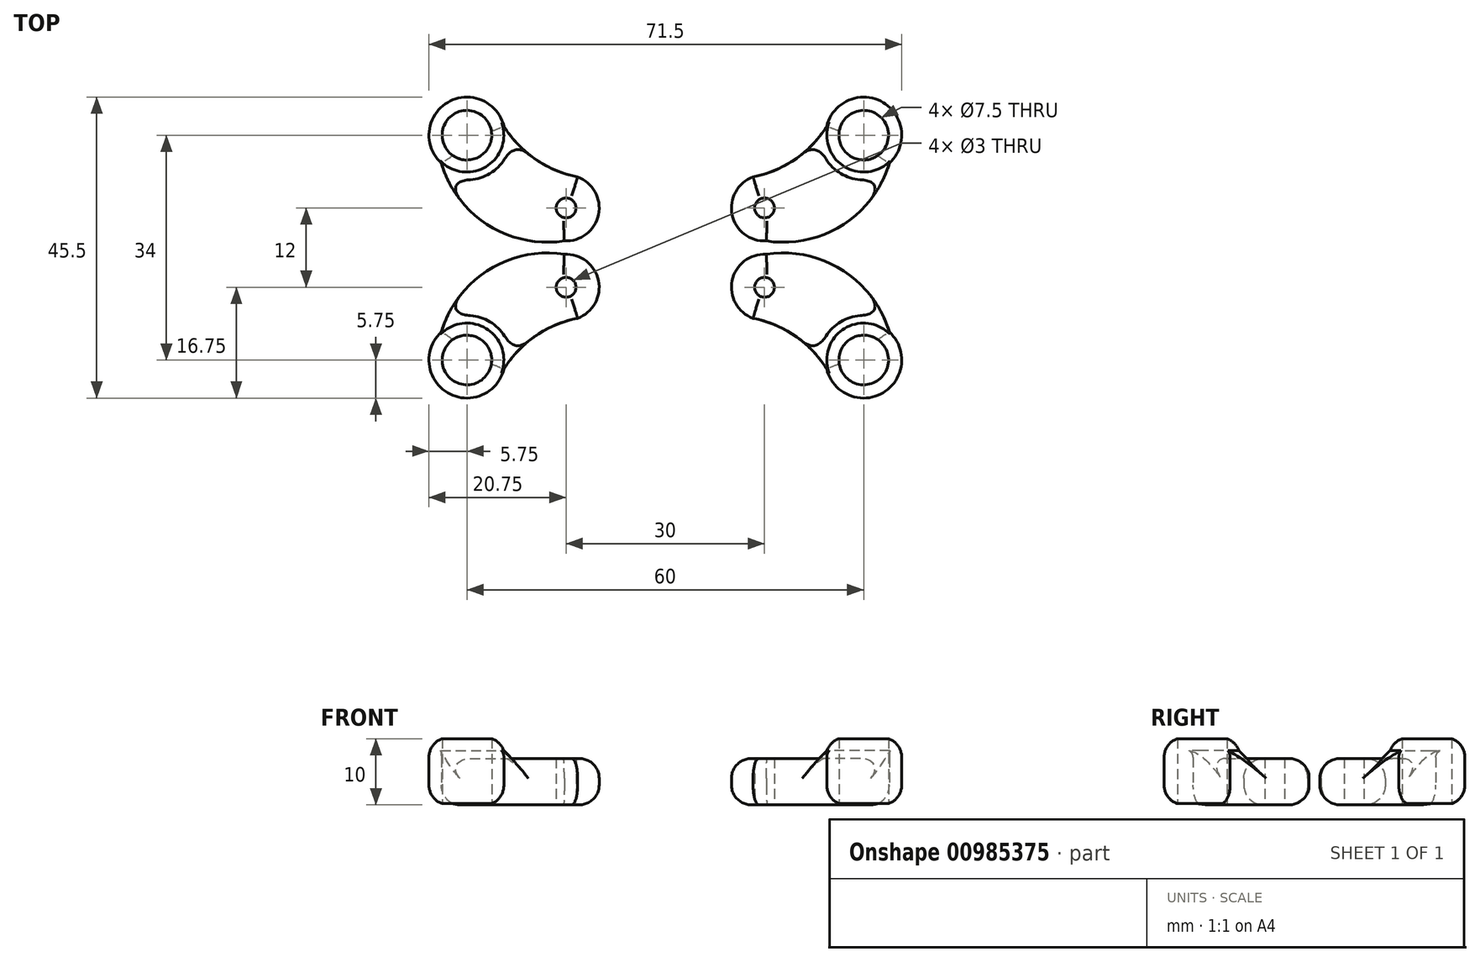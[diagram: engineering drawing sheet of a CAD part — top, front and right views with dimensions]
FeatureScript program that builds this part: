
annotation { "Feature Type Name" : "Feature", "Feature Type Description" : "" }
export const myFeature = defineFeature(function(context is Context, id is Id, definition is map)
    precondition{}
    {
        {
            var Q0;
            Q0=qCreatedBy(makeId("Top.planeOp"),FACE);
            var sketch = newSketch(context, id + "F0", { "sketchPlane" : qUnion([Q0])});
            skPoint(sketch, "E0.middle", {"position": v(0, 0) * mm});
            skCircle(sketch, "E1", {"center": v(-30, 17) * mm, "radius": 3.75 * mm});
            skCircle(sketch, "E2", {"center": v(-30, 17) * mm, "radius": 5.75 * mm});
            skCircle(sketch, "E3", {"center": v(-15, 6) * mm, "radius": 1.5 * mm});
            skCircle(sketch, "E4", {"center": v(-15, 6) * mm, "radius": 5 * mm});
            skArc(sketch, "E5", {"start": v(-25.68, 20.8) * mm, "mid": v(-20.74, 14.2) * mm, "end": v(-13.27, 10.7) * mm});
            skArc(sketch, "E6", {"start": v(-33.87, 12.75) * mm, "mid": v(-26.77, 3.4) * mm, "end": v(-15.27, 1) * mm});
            skSolve(sketch);
        }
        {
            var Q0;
            Q0=makeQuery(id+"F0.imprint","IMPRINT",FACE,{"disambiguationData":[TD([[makeQuery(id+"F0.imprint","IMPRINT",EDGE,{"derivedFrom":sQuery(id+"F0.wireOp",EDGE,"9357O7tW-9z78-CaA4-5se2-U8UIPOlfQfit.bottom")}),1.0]])]});
            var Q1;
            Q1=makeQuery(id+"F0.imprint","IMPRINT",FACE,{"disambiguationData":[TD([[makeQuery(id+"F0.imprint","IMPRINT",EDGE,{"derivedFrom":sQuery(id+"F0.wireOp",EDGE,"9357O7tW-9z78-CaA4-5se2-U8UIPOlfQfit.bottom")}),-1.0]])]});
            var Q2;
            {var subQ0=sQuery(id+"F0.wireOp",EDGE,"XfmaCdGe-Nsh5-LR8N-U050-nXJdRo87k7nu");Q2=makeQuery(id+"F0.imprint","IMPRINT",FACE,{"disambiguationData":[TD([[makeQuery(id+"F0.imprint","IMPRINT",EDGE,{"derivedFrom":subQ0}),-1.0]])]});}
            var Q3;
            {var subQ0=sQuery(id+"F0.wireOp",EDGE,"67c493aa-9df7-43f4-b791-e47cdcb916b60.MirrorCS");Q3=makeQuery(id+"F0.imprint","IMPRINT",FACE,{"disambiguationData":[TD([[makeQuery(id+"F0.imprint","IMPRINT",EDGE,{"derivedFrom":subQ0}),-1.0]])]});}
            var Q4;
            {var subQ0=sQuery(id+"F0.wireOp",EDGE,"3c266ea2-0ddf-4ded-b89f-077357a7d8e80.MirrorCS");Q4=makeQuery(id+"F0.imprint","IMPRINT",FACE,{"disambiguationData":[TD([[makeQuery(id+"F0.imprint","IMPRINT",EDGE,{"derivedFrom":subQ0}),-1.0]])]});}
            var Q5;
            {var subQ0=sQuery(id+"F0.wireOp",EDGE,"ab4d64e5-a29a-4c87-9f54-f3676ced8fba0.MirrorCS");Q5=makeQuery(id+"F0.imprint","IMPRINT",FACE,{"disambiguationData":[TD([[makeQuery(id+"F0.imprint","IMPRINT",EDGE,{"derivedFrom":subQ0}),1.0]])]});}
            var Q6;
            Q6=makeQuery(id+"F0.imprint","IMPRINT",FACE,{"disambiguationData":[TD([[makeQuery(id+"F0.imprint","IMPRINT",EDGE,{"derivedFrom":sQuery(id+"F0.wireOp",EDGE,"5d5cfb4f-1e90-434a-910e-95713f9e32be0.MirrorC")}),1.0]])]});
            var Q7;
            Q7=makeQuery(id+"F0.imprint","IMPRINT",FACE,{"disambiguationData":[TD([[makeQuery(id+"F0.imprint","IMPRINT",EDGE,{"derivedFrom":sQuery(id+"F0.wireOp",EDGE,"24c43ebd-9ed0-4dd5-8c82-3635907a6bdc0.MirrorC")}),-1.0]])]});
            var Q8;
            Q8=makeQuery(id+"F0.imprint","IMPRINT",FACE,{"disambiguationData":[TD([[makeQuery(id+"F0.imprint","IMPRINT",EDGE,{"derivedFrom":sQuery(id+"F0.wireOp",EDGE,"ed7e95fd-fa47-4424-be7c-35b6ced3335c0.MirrorC")}),1.0]])]});
            var Q9;
            Q9=makeQuery(id+"F0.imprint","IMPRINT",FACE,{"disambiguationData":[TD([[makeQuery(id+"F0.imprint","IMPRINT",EDGE,{"derivedFrom":sQuery(id+"F0.wireOp",EDGE,"sMkcqQPm-D7Am-9ELx-zUy6-8poXXiJyxJ4t")}),-1.0]])]});
            var Q10;
            {var subQ2=sQuery(id+"F0.wireOp",EDGE,"X9ugOP2y-zs2E-4G1d-y63R-nyf2ct76moEV");Q10=makeQuery(id+"F0.imprint","IMPRINT",FACE,{"disambiguationData":[TD([[makeQuery(id+"F0.imprint","IMPRINT",EDGE,{"derivedFrom":subQ2}),-1.0]])]});}
            var Q11;
            {var subQ0=sQuery(id+"F0.wireOp",EDGE,"BiexqiD6-ktly-UjJq-ChZm-LXQvsZC7DSTw");Q11=makeQuery(id+"F0.imprint","IMPRINT",FACE,{"disambiguationData":[TD([[makeQuery(id+"F0.imprint","IMPRINT",EDGE,{"derivedFrom":subQ0}),1.0]])]});}
            var Q12;
            {var subQ2=sQuery(id+"F0.wireOp",EDGE,"diys7w2P-Qjjo-Jf2j-Kp6D-45MT6dFCwVuy");var subQ7=sQuery(id+"F0.wireOp",EDGE,"E1");var subQ8=makeQuery(id+"F0.imprint","INTERSECT",VERTEX,{"derivedFrom":[subQ7,subQ2]});Q12=makeQuery(id+"F0.imprint","IMPRINT",FACE,{"disambiguationData":[TD([[makeQuery(id+"F0.imprint","IMPRINT",EDGE,{"disambiguationData":[TD([[subQ8,-1.0]])],"derivedFrom":subQ7}),-1.0]])]});}
            var Q13;
            {var subQ0=sQuery(id+"F0.wireOp",EDGE,"E6");Q13=makeQuery(id+"F0.imprint","IMPRINT",FACE,{"disambiguationData":[TD([[makeQuery(id+"F0.imprint","IMPRINT",EDGE,{"derivedFrom":subQ0}),1.0]])]});}
            var Q14;
            Q14=makeQuery(id+"F0.imprint","IMPRINT",FACE,{"disambiguationData":[TD([[makeQuery(id+"F0.imprint","IMPRINT",EDGE,{"derivedFrom":sQuery(id+"F0.wireOp",EDGE,"E3")}),-1.0]])]});
            extrude(context, id + "F1", {"entities" : qUnion([Q0, Q1, Q2, Q3, Q4, Q5, Q6, Q7, Q8, Q9, Q10, Q11, Q12, Q13, Q14]), "depth" : 7 * mm, "offsetDistance" : 25 * mm});
        }
        {
            var Q0;
            Q0=makeQuery(id+"F0.imprint","IMPRINT",FACE,{"disambiguationData":[TD([[makeQuery(id+"F0.imprint","IMPRINT",EDGE,{"derivedFrom":sQuery(id+"F0.wireOp",EDGE,"5d5cfb4f-1e90-434a-910e-95713f9e32be0.MirrorC")}),1.0]])]});
            var Q1;
            Q1=makeQuery(id+"F0.imprint","IMPRINT",FACE,{"disambiguationData":[TD([[makeQuery(id+"F0.imprint","IMPRINT",EDGE,{"derivedFrom":sQuery(id+"F0.wireOp",EDGE,"24c43ebd-9ed0-4dd5-8c82-3635907a6bdc0.MirrorC")}),-1.0]])]});
            var Q2;
            Q2=makeQuery(id+"F0.imprint","IMPRINT",FACE,{"disambiguationData":[TD([[makeQuery(id+"F0.imprint","IMPRINT",EDGE,{"derivedFrom":sQuery(id+"F0.wireOp",EDGE,"ed7e95fd-fa47-4424-be7c-35b6ced3335c0.MirrorC")}),1.0]])]});
            var Q3;
            {var subQ2=sQuery(id+"F0.wireOp",EDGE,"diys7w2P-Qjjo-Jf2j-Kp6D-45MT6dFCwVuy");var subQ7=sQuery(id+"F0.wireOp",EDGE,"E1");var subQ8=makeQuery(id+"F0.imprint","INTERSECT",VERTEX,{"derivedFrom":[subQ7,subQ2]});Q3=makeQuery(id+"F0.imprint","IMPRINT",FACE,{"disambiguationData":[TD([[makeQuery(id+"F0.imprint","IMPRINT",EDGE,{"disambiguationData":[TD([[subQ8,-1.0]])],"derivedFrom":subQ7}),-1.0]])]});}
            var Q4;
            {var subQ0=sQuery(id+"F0.wireOp",EDGE,"E5");var subQ1=sQuery(id+"F0.wireOp",EDGE,"E2");var subQ2=makeQuery(id+"F0.imprint","INTERSECT",VERTEX,{"disambiguationData":[OD(0.0)],"derivedFrom":[subQ1,subQ0]});Q4=makeQuery(id+"F0.imprint","IMPRINT",FACE,{"disambiguationData":[TD([[makeQuery(id+"F0.imprint","IMPRINT",EDGE,{"disambiguationData":[TD([[subQ2,1.0]])],"derivedFrom":subQ1}),1.0]])]});}
            extrude(context, id + "F2", {"entities" : qUnion([Q0, Q1, Q2, Q3, Q4]), "operationType" : NewBodyOperationType.ADD, "depth" : 10 * mm, "offsetDistance" : 25 * mm});
        }
        {
            var Q0;
            {var subQ0=sQuery(id+"F0.wireOp",EDGE,"CDqiK6rF-uQFd-2Xwm-xQsp-tWEG5a64DqiY");var subQ1=sQuery(id+"F0.wireOp",EDGE,"E2");var subQ2=makeQuery(id+"F0.imprint","INTERSECT",VERTEX,{"derivedFrom":[subQ1,subQ0]});Q0=makeQuery(id+"F0.imprint","IMPRINT",FACE,{"disambiguationData":[TD([[makeQuery(id+"F0.imprint","IMPRINT",EDGE,{"disambiguationData":[TD([[subQ2,-1.0]])],"derivedFrom":subQ1}),-1.0]])]});}
            var Q1;
            {var subQ0=sQuery(id+"F0.wireOp",EDGE,"diys7w2P-Qjjo-Jf2j-Kp6D-45MT6dFCwVuy");var subQ1=sQuery(id+"F0.wireOp",EDGE,"E1");var subQ2=makeQuery(id+"F0.imprint","INTERSECT",VERTEX,{"derivedFrom":[subQ1,subQ0]});Q1=makeQuery(id+"F0.imprint","IMPRINT",FACE,{"disambiguationData":[TD([[makeQuery(id+"F0.imprint","IMPRINT",EDGE,{"disambiguationData":[TD([[subQ2,1.0]])],"derivedFrom":subQ1}),-1.0]])]});}
            var Q2;
            {var subQ0=sQuery(id+"F0.wireOp",EDGE,"X9ugOP2y-zs2E-4G1d-y63R-nyf2ct76moEV");Q2=makeQuery(id+"F0.imprint","IMPRINT",FACE,{"disambiguationData":[TD([[makeQuery(id+"F0.imprint","IMPRINT",EDGE,{"derivedFrom":subQ0}),1.0]])]});}
            extrude(context, id + "F3", {"entities" : qUnion([Q0, Q1, Q2]), "operationType" : NewBodyOperationType.ADD, "depth" : 2 * mm, "offsetDistance" : 25 * mm});
        }
        {
            var Q0;
            {var subQ0=sQuery(id+"F0.wireOp",EDGE,"E2");Q0=makeQuery(id+"F2.boolean.opBoolean","INTERSECT",EDGE,{"derivedFrom":[makeQuery(id+"F1.opExtrude","CAP_FACE",FACE,{"disambiguationData":[OSD([sQuery(id+"F0.wireOp",EDGE,"E1"),subQ0,sQuery(id+"F0.wireOp",EDGE,"E3"),sQuery(id+"F0.wireOp",EDGE,"E4"),sQuery(id+"F0.wireOp",EDGE,"E5"),sQuery(id+"F0.wireOp",EDGE,"E6")])],"isStart":false}),makeQuery(id+"F2.opExtrude","SWEPT_FACE",FACE,{"disambiguationData":[OSD([subQ0])]})]});}
            chamfer(context, id + "F4", {"entities" : qUnion([Q0]), "width" : 1 * mm, "tangentPropagation" : true});
        }
        {
            var Q0;
            Q0=makeQuery(id+"F2.opExtrude","CAP_EDGE",EDGE,{"disambiguationData":[OSD([sQuery(id+"F0.wireOp",EDGE,"E2")])],"isStart":false});
            var Q1;
            Q1=makeQuery(id+"F1.opExtrude","CAP_EDGE",EDGE,{"disambiguationData":[OSD([sQuery(id+"F0.wireOp",EDGE,"E6")])],"isStart":true});
            var Q2;
            {var subQ0=sQuery(id+"F0.wireOp",EDGE,"E2");Q2=makeQuery(id+"F2.boolean.opBoolean","MERGE",EDGE,{"derivedFrom":[makeQuery(id+"F1.opExtrude","CAP_EDGE",EDGE,{"disambiguationData":[OSD([subQ0])],"isStart":true}),makeQuery(id+"F2.opExtrude","CAP_EDGE",EDGE,{"disambiguationData":[OSD([subQ0])],"isStart":true})]});}
            var Q3;
            Q3=makeQuery(id+"F1.opExtrude","CAP_EDGE",EDGE,{"disambiguationData":[OSD([sQuery(id+"F0.wireOp",EDGE,"E5")])],"isStart":true});
            var Q4;
            Q4=makeQuery(id+"F1.opExtrude","CAP_EDGE",EDGE,{"disambiguationData":[OSD([sQuery(id+"F0.wireOp",EDGE,"E4")])],"isStart":true});
            var Q5;
            Q5=makeQuery(id+"F1.opExtrude","CAP_EDGE",EDGE,{"disambiguationData":[OSD([sQuery(id+"F0.wireOp",EDGE,"E4")])],"isStart":false});
            var Q6;
            Q6=makeQuery(id+"F1.opExtrude","CAP_EDGE",EDGE,{"disambiguationData":[OSD([sQuery(id+"F0.wireOp",EDGE,"E6")])],"isStart":false});
            var Q7;
            Q7=makeQuery(id+"F1.opExtrude","CAP_EDGE",EDGE,{"disambiguationData":[OSD([sQuery(id+"F0.wireOp",EDGE,"E5")])],"isStart":false});
            fillet(context, id + "F5", {"entities" : qUnion([Q0, Q1, Q2, Q3, Q4, Q5, Q6, Q7]), "radius" : 3 * mm, "tangentPropagation" : true, "allowEdgeOverflow" : false});
        }
        {
            var Q0;
            Q0=makeQuery(id+"F1.opExtrude","SWEPT_BODY",BODY,{"disambiguationData":[OSD([sQuery(id+"F0.wireOp",EDGE,"E1"),sQuery(id+"F0.wireOp",EDGE,"E2"),sQuery(id+"F0.wireOp",EDGE,"E3"),sQuery(id+"F0.wireOp",EDGE,"E4"),sQuery(id+"F0.wireOp",EDGE,"E5"),sQuery(id+"F0.wireOp",EDGE,"E6")])]});
            var Q1;
            Q1=qCreatedBy(makeId("Right.planeOp"),FACE);
            mirror(context, id + "F6", {"entities" : qUnion([Q0]), "mirrorPlane" : qUnion([Q1])});
        }
        {
            var Q0;
            Q0=makeQuery(id+"F1.opExtrude","SWEPT_BODY",BODY,{"disambiguationData":[OSD([sQuery(id+"F0.wireOp",EDGE,"E1"),sQuery(id+"F0.wireOp",EDGE,"E2"),sQuery(id+"F0.wireOp",EDGE,"E3"),sQuery(id+"F0.wireOp",EDGE,"E4"),sQuery(id+"F0.wireOp",EDGE,"E5"),sQuery(id+"F0.wireOp",EDGE,"E6")])]});
            var Q1;
            Q1=makeQuery(id+"F6.opPattern","COPY",BODY,{"derivedFrom":makeQuery(id+"F1.opExtrude","SWEPT_BODY",BODY,{"disambiguationData":[OSD([sQuery(id+"F0.wireOp",EDGE,"E1"),sQuery(id+"F0.wireOp",EDGE,"E2"),sQuery(id+"F0.wireOp",EDGE,"E3"),sQuery(id+"F0.wireOp",EDGE,"E4"),sQuery(id+"F0.wireOp",EDGE,"E5"),sQuery(id+"F0.wireOp",EDGE,"E6")])]}),"instanceName":"1"});
            var Q2;
            Q2=qCreatedBy(makeId("Front.planeOp"),FACE);
            mirror(context, id + "F7", {"entities" : qUnion([Q0, Q1]), "mirrorPlane" : qUnion([Q2])});
        }
    });
